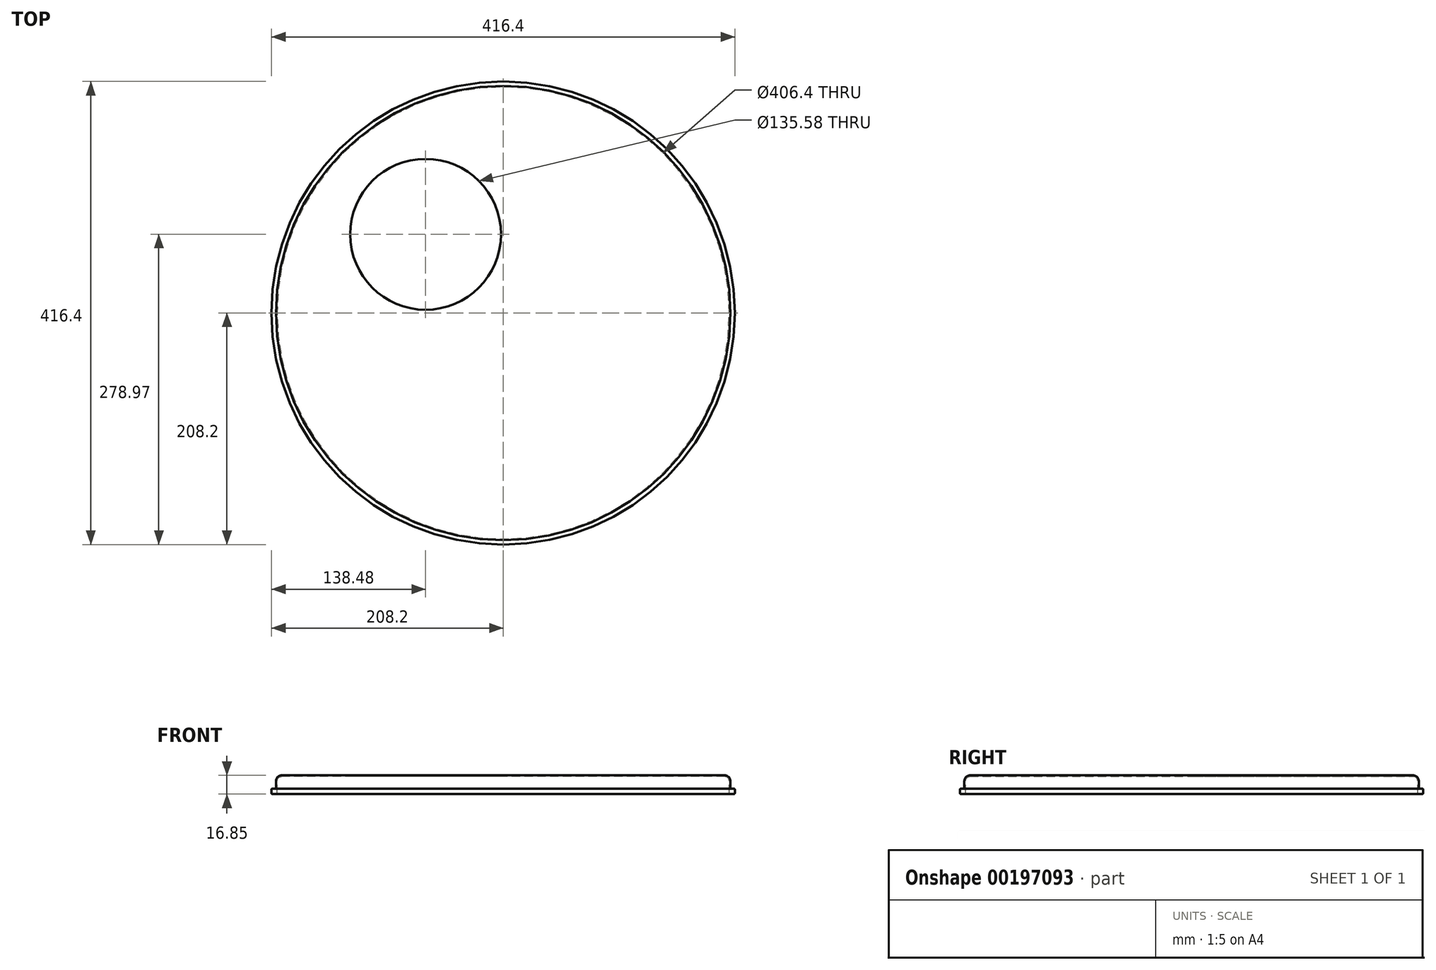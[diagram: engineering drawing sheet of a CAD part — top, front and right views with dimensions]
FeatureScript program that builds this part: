
annotation { "Feature Type Name" : "Feature", "Feature Type Description" : "" }
export const myFeature = defineFeature(function(context is Context, id is Id, definition is map)
    precondition{}
    {
        {
            var Q0;
            Q0=qCreatedBy(makeId("Front.planeOp"),FACE);
            var sketch = newSketch(context, id + "F0", { "sketchPlane" : qUnion([Q0])});
            skLineSegment(sketch, "E0", {"start": v(0, 0) * mm, "end": v(-199.2, 0) * mm});
            skLineSegment(sketch, "E1", {"start": v(-203.2, -4) * mm, "end": v(-203.2, -10.85) * mm});
            skArc(sketch, "E2", {"start": v(-199.2, 0) * mm, "mid": v(-202.03, -1.17) * mm, "end": v(-203.2, -4) * mm});
            skLineSegment(sketch, "E3", {"start": v(-203.2, -10.85) * mm, "end": v(-203.2, -14.85) * mm});
            skLineSegment(sketch, "E4", {"start": v(-204.2, -15.85) * mm, "end": v(-207.2, -15.85) * mm});
            skLineSegment(sketch, "E5", {"start": v(-208.2, -14.85) * mm, "end": v(-208.2, -11.85) * mm});
            skLineSegment(sketch, "E6", {"start": v(-207.2, -10.85) * mm, "end": v(-204.2, -10.85) * mm});
            skPoint(sketch, "E7.visualSharp", {"position": v(-208.2, -10.85) * mm});
            skArc(sketch, "E7.filletArc", {"start": v(-207.2, -10.85) * mm, "mid": v(-207.9, -11.14) * mm, "end": v(-208.2, -11.85) * mm});
            skPoint(sketch, "E8.visualSharp", {"position": v(-208.2, -15.85) * mm});
            skArc(sketch, "E8.filletArc", {"start": v(-208.2, -14.85) * mm, "mid": v(-207.9, -15.55) * mm, "end": v(-207.2, -15.85) * mm});
            skPoint(sketch, "E9.visualSharp", {"position": v(-203.2, -15.85) * mm});
            skArc(sketch, "E9.filletArc", {"start": v(-204.2, -15.85) * mm, "mid": v(-203.5, -15.55) * mm, "end": v(-203.2, -14.85) * mm});
            skLineSegment(sketch, "E10", {"start": v(-204.2, -10.85) * mm, "end": v(-204.2, -4) * mm});
            skArc(sketch, "E11.0", {"start": v(-199.2, 1) * mm, "mid": v(-202.74, -0.46) * mm, "end": v(-204.2, -4) * mm});
            skLineSegment(sketch, "E12", {"start": v(-199.2, 1) * mm, "end": v(0, 1) * mm});
            skLineSegment(sketch, "E13", {"start": v(0, 1) * mm, "end": v(0, 0) * mm});
            skSolve(sketch);
        }
        {
            var Q0;
            Q0=makeQuery(id+"F0.imprint","IMPRINT",FACE,{"disambiguationData":[TD([[makeQuery(id+"F0.imprint","IMPRINT",EDGE,{"derivedFrom":sQuery(id+"F0.wireOp",EDGE,"E0")}),-1.0]])]});
            var Q1;
            Q1=sQuery(id+"F0.wireOp",EDGE,"E13");
            revolve(context, id + "F1", {"entities" : qUnion([Q0]), "axis" : qUnion([Q1]), "revolveType" : RevolveType.FULL});
        }
        {
            var Q0;
            Q0=makeQuery(id+"F1.opRevolve","SWEPT_FACE",FACE,{"disambiguationData":[OSD([sQuery(id+"F0.wireOp",EDGE,"E12")])]});
            var sketch = newSketch(context, id + "F2", { "sketchPlane" : qUnion([Q0])});
            skCircle(sketch, "E14", {"center": v(-69.72, 70.77) * mm, "radius": 67.8 * mm});
            skSolve(sketch);
        }
        {
            var Q0;
            Q0 = qSketchRegion(id + "F2", true);
            extrude(context, id + "F3", {"entities" : qUnion([Q0]), "operationType" : NewBodyOperationType.REMOVE, "endBound" : BoundingType.THROUGH_ALL, "oppositeDirection" : true, "depth" : 25 * mm});
        }
    });
